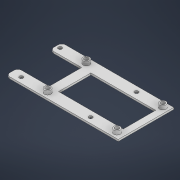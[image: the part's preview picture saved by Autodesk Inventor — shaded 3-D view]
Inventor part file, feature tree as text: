
AUTODESK INVENTOR PART (.ipt)
format: ipt  version: 2021 (Build 250183000, 183)  size: 190,976 bytes
history: native  units: mm
features: extrude x6, sketch x5, fillet x1
ambient origin geometry x8: Origin, YZ Plane, XZ Plane, XY Plane, X Axis, Y Axis, Z Axis, Center Point
bodies: Volumenkörper1 (feature_tree)
feature tree (12):
  extrude  "Extrusion1"  Depth=60.0mm
  sketch  "Skizze2"  dims[d2=2.0mm d3=0.0mm d4=4.5mm]
  extrude  "Extrusion2"  Depth=2.0mm
  extrude  "Extrusion3"  Depth=15.24mm
  extrude  "Extrusion4"  Depth=24.13mm
  extrude  "Extrusion5"  Depth=4.0mm
  extrude  "Extrusion6"  Depth=4.0mm
  fillet  "Rundung1"  Radius=82.55mm
  sketch  "Skizze1"  dims[d0=130.0mm d1=60.0mm]
  sketch  "Skizze3"  dims[d5=24.13mm d6=15.24mm]
  sketch  "Skizze4"  dims[d7=4.5mm d8=24.13mm]
  sketch  "Skizze5"  dims[d9=13.97mm d10=4.5mm d11=24.13mm d12=82.55mm d13=4.5mm d14=24.13mm d15=74.93mm d16=4.0mm d17=4.0mm d18=4.0mm d19=82.55mm d20=4.0mm d21=74.93mm d22=24.13mm d23=24.13mm d24=11.392317mm d25=5.042317mm d26=24.13mm d27=24.13mm d28=2.0mm d29=0.0mm d30=35.0mm d31=35.0mm d32=2.0mm d33=0.0mm d34=1.0mm d35=0.0mm d36=70.0mm d37=35.0mm d38=15.0mm d39=8.0mm d40=0.0mm d41=7.0mm d42=7.0mm d43=7.0mm d44=7.0mm d45=4.0mm d46=0.0mm d47=4.0mm]
